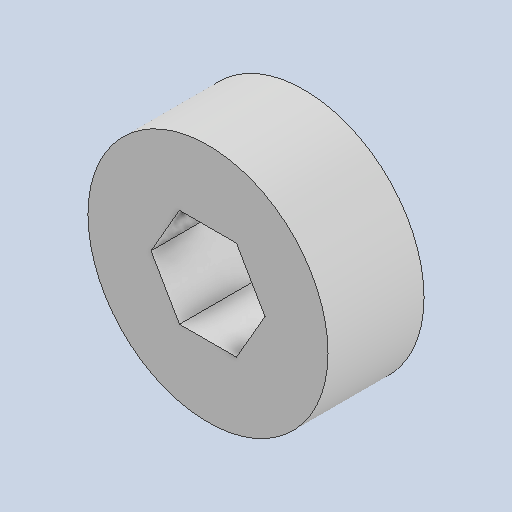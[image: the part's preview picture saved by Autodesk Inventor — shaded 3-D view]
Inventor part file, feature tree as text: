
AUTODESK INVENTOR PART (.ipt)
format: ipt  version: 2022 (Build 260153000, 153)  size: 124,416 bytes
history: native  units: mm
features: reference x7, other x4, extrude x2, sketch x1
ambient origin geometry x8: Origin, YZ Plane, XZ Plane, XY Plane, X Axis, Y Axis, Z Axis, Center Point
bodies: Solid1 (feature_tree)
feature tree (14):
  extrude  "Extrusion1"  Depth=10.0mm
  extrude  "Extrusion2"  Depth=10.0mm TaperAngle=360.0deg
  reference  "Reference1"
  reference  "Reference2"
  reference  "Reference3"
  reference  "Reference4"
  reference  "Reference5"
  reference  "Reference6"
  sketch  "Sketch2"  dims[d1=6.0mm d2=0.0mm d4=3.1mm d5=60.0mm d7=360.0deg d9=0.4mm d10=10.0mm d11=0.0mm]
  reference  "Reference7"
  other  "Caja_Reductora.iam"
  other  "Hombro_Ejes:6"
  other  "Caja_Reductora_.iam"
  other  "Rodamiento_Ejes:6"
